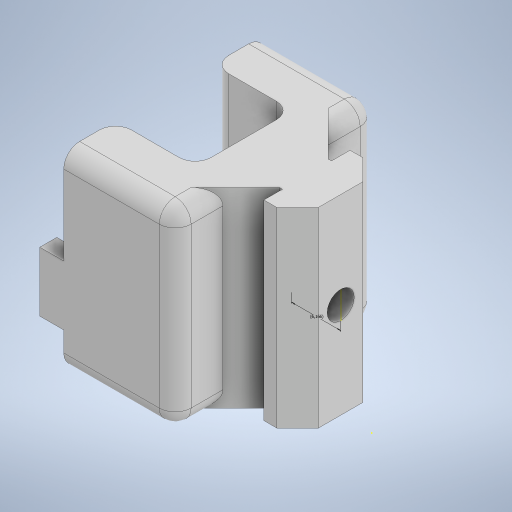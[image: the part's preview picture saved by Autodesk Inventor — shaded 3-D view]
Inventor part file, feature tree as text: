
AUTODESK INVENTOR PART (.ipt)
format: ipt  version: 2023 (Build 270158000, 158)  size: 756,224 bytes
history: native  units: mm
features: sketch x7, extrude x6, other x1, fillet x1, projected_geometry x1
ambient origin geometry x8: Origin, YZ Plane, XZ Plane, XY Plane, X Axis, Y Axis, Z Axis, Center Point
bodies: Body1 (feature_tree), Body2 (feature_tree)
feature tree (16):
  other  "Bryła1"
  extrude  "Wyciągnięcie proste1"  Depth=5.582349mm
  extrude  "Wyciągnięcie proste5"  TaperAngle=135.0deg  [1 undecoded]
  extrude  "Wyciągnięcie proste6"  TaperAngle=135.0deg  [1 undecoded]
  sketch  "Szkic15"
  sketch  "Szkic16"
  extrude  "Wyciągnięcie proste7"  Depth=1.6154mm
  sketch  "Szkic18"
  extrude  "Wyciągnięcie proste8"  Depth=2.615175mm
  extrude  "Wyciągnięcie proste9"  Depth=2.328242mm
  fillet  "Zaokrąglenie1"  Radius=24.0mm
  sketch  "Szkic3"
  sketch  "Szkic13"
  sketch  "Szkic14"
  projected_geometry  "Pętla rzutowana1"
  sketch  "Szkic17"
note: 2 required parameter values undecoded (feature->parameter linkage not recoverable at this tier; creation-order binding heuristic only, values carry confidence <= 0.55)
